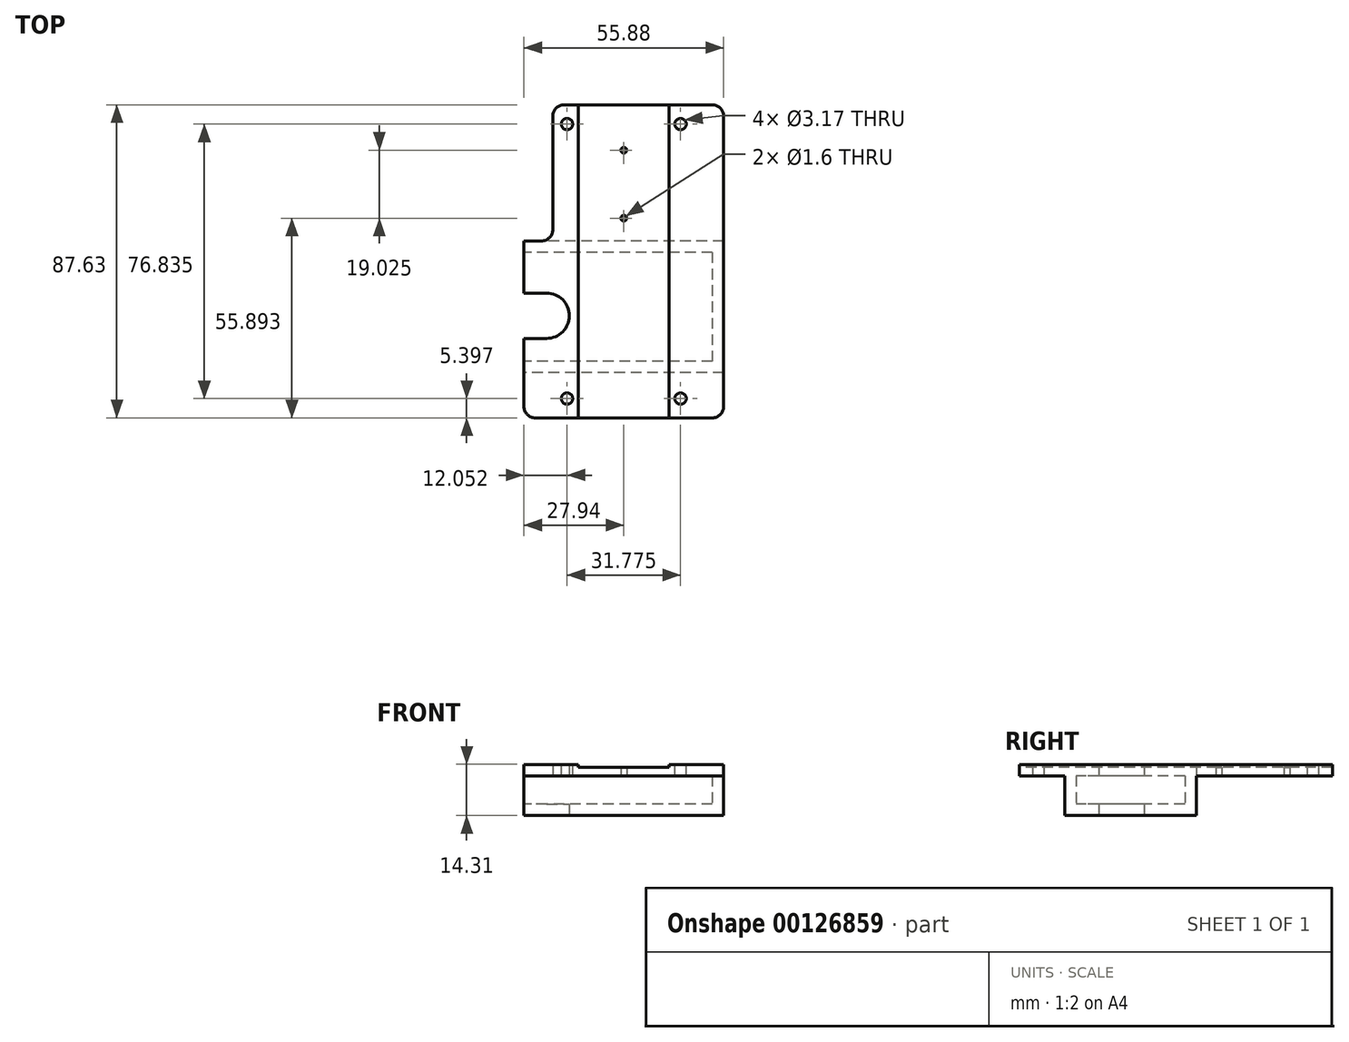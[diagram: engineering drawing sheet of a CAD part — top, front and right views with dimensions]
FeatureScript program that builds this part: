
annotation { "Feature Type Name" : "Feature", "Feature Type Description" : "" }
export const myFeature = defineFeature(function(context is Context, id is Id, definition is map)
    precondition{}
    {
        {
            var Q0;
            Q0=qCreatedBy(makeId("Top.planeOp"),FACE);
            var sketch = newSketch(context, id + "F0", { "sketchPlane" : qUnion([Q0])});
            skLineSegment(sketch, "E0.rect.top", {"start": v(27.94, 0) * mm, "end": v(-27.94, 0) * mm});
            skLineSegment(sketch, "E0.rect.left", {"start": v(27.94, 74.93) * mm, "end": v(27.94, 0) * mm});
            skLineSegment(sketch, "E0.rect.right", {"start": v(-27.94, 36.83) * mm, "end": v(-27.94, 0) * mm});
            skPoint(sketch, "E0.rect.middle", {"position": v(0, 0) * mm});
            skLineSegment(sketch, "E1", {"start": v(-27.94, 36.83) * mm, "end": v(27.94, 36.83) * mm, "construction": true});
            skCircle(sketch, "E2", {"center": v(0, 43.2) * mm, "radius": 0.8 * mm});
            skCircle(sketch, "E3", {"center": v(0, 62.22) * mm, "radius": 0.8 * mm});
            skLineSegment(sketch, "E4", {"start": v(0, 43.2) * mm, "end": v(0, 62.22) * mm, "construction": true});
            skPoint(sketch, "E5", {"position": v(0, 52.7) * mm});
            skLineSegment(sketch, "E6.bottom", {"start": v(14.29, 65.4) * mm, "end": v(-14.29, 65.4) * mm, "construction": true});
            skLineSegment(sketch, "E6.top", {"start": v(14.29, 40) * mm, "end": v(-14.29, 40) * mm, "construction": true});
            skLineSegment(sketch, "E6.left", {"start": v(14.29, 65.4) * mm, "end": v(14.29, 40) * mm, "construction": true});
            skLineSegment(sketch, "E6.right", {"start": v(-14.29, 65.4) * mm, "end": v(-14.29, 40) * mm, "construction": true});
            skLineSegment(sketch, "E7", {"start": v(-19.88, 74.93) * mm, "end": v(27.94, 74.93) * mm});
            skLineSegment(sketch, "E8.bottom", {"start": v(-19.88, 36.83) * mm, "end": v(-27.94, 36.83) * mm});
            skLineSegment(sketch, "E8.left", {"start": v(-19.88, 36.83) * mm, "end": v(-19.88, 74.93) * mm});
            skSolve(sketch);
        }
        {
            var Q0;
            Q0=qSketchRegion(id+"F0",true);
            extrude(context, id + "F1", {"entities" : qUnion([Q0]), "depth" : 3.17 * mm});
        }
        {
            var Q0;
            Q0=makeQuery(id+"F1.opExtrude","CAP_FACE",FACE,{"disambiguationData":[OSD([sQuery(id+"F0.wireOp",EDGE,"E0.rect.bottom"),sQuery(id+"F0.wireOp",EDGE,"E0.rect.top"),sQuery(id+"F0.wireOp",EDGE,"E0.rect.left"),sQuery(id+"F0.wireOp",EDGE,"E0.rect.right")])],"isStart":true});
            var sketch = newSketch(context, id + "F2", { "sketchPlane" : qUnion([Q0])});
            skLineSegment(sketch, "E9.bottom", {"start": v(-27.94, 0) * mm, "end": v(27.94, 0) * mm});
            skLineSegment(sketch, "E9.top", {"start": v(-27.94, -36.83) * mm, "end": v(27.94, -36.83) * mm});
            skLineSegment(sketch, "E9.left", {"start": v(-27.94, 0) * mm, "end": v(-27.94, -36.83) * mm});
            skLineSegment(sketch, "E9.right", {"start": v(27.94, 0) * mm, "end": v(27.94, -36.83) * mm});
            skPoint(sketch, "E10", {"position": v(0, 0) * mm});
            skSolve(sketch);
        }
        {
            var Q0;
            Q0=qSketchRegion(id+"F2",true);
            extrude(context, id + "F3", {"entities" : qUnion([Q0]), "operationType" : NewBodyOperationType.ADD, "depth" : 11.13 * mm});
        }
        {
            var Q0;
            Q0=makeQuery(id+"F3.opExtrude","CAP_FACE",FACE,{"disambiguationData":[OSD([sQuery(id+"F2.wireOp",EDGE,"E9.bottom"),sQuery(id+"F2.wireOp",EDGE,"E9.top"),sQuery(id+"F2.wireOp",EDGE,"E9.left"),sQuery(id+"F2.wireOp",EDGE,"E9.right")])],"isStart":false});
            var sketch = newSketch(context, id + "F4", { "sketchPlane" : qUnion([Q0])});
            skLineSegment(sketch, "E11", {"start": v(-27.94, -22.23) * mm, "end": v(-27.94, -9.53) * mm});
            skLineSegment(sketch, "E12", {"start": v(-27.94, -9.52) * mm, "end": v(-21.6, -9.52) * mm});
            skLineSegment(sketch, "E13", {"start": v(-27.94, -22.22) * mm, "end": v(-21.6, -22.22) * mm});
            skArc(sketch, "E14", {"start": v(-21.6, -22.22) * mm, "mid": v(-15.24, -15.88) * mm, "end": v(-21.6, -9.53) * mm});
            skSolve(sketch);
        }
        {
            var Q0;
            Q0=qSketchRegion(id+"F4",true);
            extrude(context, id + "F5", {"entities" : qUnion([Q0]), "operationType" : NewBodyOperationType.REMOVE, "endBound" : BoundingType.THROUGH_ALL, "oppositeDirection" : true, "depth" : 25.4 * mm});
        }
        {
            var Q0;
            {var subQ0=sQuery(id+"F0.wireOp",EDGE,"E0.rect.right");var subQ1=sQuery(id+"F0.wireOp",EDGE,"E0.rect.top");var subQ2=sQuery(id+"F2.wireOp",EDGE,"E9.left");Q0=makeQuery(id+"F5.boolean.opBoolean","SPLIT",FACE,{"disambiguationData":[TD([makeQuery(id+"F1.opExtrude","SWEPT_FACE",FACE,{"disambiguationData":[OSD([subQ1])]})])],"derivedFrom":makeQuery(id+"F3.boolean.opBoolean","MERGE",FACE,{"derivedFrom":[makeQuery(id+"F1.opExtrude","SWEPT_FACE",FACE,{"disambiguationData":[OSD([subQ0])]}),makeQuery(id+"F3.opExtrude","SWEPT_FACE",FACE,{"disambiguationData":[OSD([subQ2])]})]})});}
            var sketch = newSketch(context, id + "F6", { "sketchPlane" : qUnion([Q0])});
            skLineSegment(sketch, "E15.bottom", {"start": v(-33.66, 0) * mm, "end": v(-3.18, 0) * mm});
            skLineSegment(sketch, "E15.top", {"start": v(-33.66, -7.95) * mm, "end": v(-3.18, -7.95) * mm});
            skLineSegment(sketch, "E15.left", {"start": v(-33.66, 0) * mm, "end": v(-33.66, -7.95) * mm});
            skLineSegment(sketch, "E15.right", {"start": v(-3.18, 0) * mm, "end": v(-3.18, -7.95) * mm});
            skSolve(sketch);
        }
        {
            var Q0;
            Q0 = qSketchRegion(id + "F6", true);
            extrude(context, id + "F7", {"entities" : qUnion([Q0]), "operationType" : NewBodyOperationType.REMOVE, "oppositeDirection" : true, "depth" : 52.7 * mm});
        }
        {
            var Q0;
            Q0=makeQuery(id+"F3.boolean.opBoolean","MERGE",FACE,{"derivedFrom":[makeQuery(id+"F1.opExtrude","SWEPT_FACE",FACE,{"disambiguationData":[OSD([sQuery(id+"F0.wireOp",EDGE,"E0.rect.top")])]}),makeQuery(id+"F3.opExtrude","SWEPT_FACE",FACE,{"disambiguationData":[OSD([sQuery(id+"F2.wireOp",EDGE,"E9.bottom")])]})]});
            var sketch = newSketch(context, id + "F8", { "sketchPlane" : qUnion([Q0])});
            skLineSegment(sketch, "E16.bottom", {"start": v(-27.94, 3.18) * mm, "end": v(27.94, 3.18) * mm});
            skLineSegment(sketch, "E16.top", {"start": v(-27.94, 0) * mm, "end": v(27.94, 0) * mm});
            skLineSegment(sketch, "E16.left", {"start": v(-27.94, 3.18) * mm, "end": v(-27.94, 0) * mm});
            skLineSegment(sketch, "E16.right", {"start": v(27.94, 3.18) * mm, "end": v(27.94, 0) * mm});
            skSolve(sketch);
        }
        {
            var Q0;
            Q0 = qSketchRegion(id + "F8", true);
            extrude(context, id + "F9", {"entities" : qUnion([Q0]), "operationType" : NewBodyOperationType.ADD, "depth" : 12.7 * mm});
        }
        {
            var Q0;
            Q0=makeQuery(id+"F3.opExtrude","CAP_EDGE",EDGE,{"disambiguationData":[OSD([sQuery(id+"F2.wireOp",EDGE,"E9.top")])],"isStart":true});
            var Q1;
            Q1=makeQuery(id+"F1.opExtrude","SWEPT_EDGE",EDGE,{"disambiguationData":[OSD([sQuery(id+"F0.wireOp",EDGE,"E8.bottom"),sQuery(id+"F0.wireOp",EDGE,"E8.left")])]});
            var Q2;
            Q2=makeQuery(id+"F1.opExtrude","SWEPT_EDGE",EDGE,{"disambiguationData":[OSD([sQuery(id+"F0.wireOp",EDGE,"E7"),sQuery(id+"F0.wireOp",EDGE,"E8.left")])]});
            var Q3;
            Q3=makeQuery(id+"F1.opExtrude","SWEPT_EDGE",EDGE,{"disambiguationData":[OSD([sQuery(id+"F0.wireOp",EDGE,"E0.rect.left"),sQuery(id+"F0.wireOp",EDGE,"E7")])]});
            var Q4;
            Q4=makeQuery(id+"F9.opExtrude","CAP_EDGE",EDGE,{"disambiguationData":[OSD([sQuery(id+"F8.wireOp",EDGE,"E16.top")])],"isStart":true});
            var Q5;
            Q5=makeQuery(id+"F9.opExtrude","CAP_EDGE",EDGE,{"disambiguationData":[OSD([sQuery(id+"F8.wireOp",EDGE,"E16.left")])],"isStart":false});
            var Q6;
            Q6=makeQuery(id+"F9.opExtrude","CAP_EDGE",EDGE,{"disambiguationData":[OSD([sQuery(id+"F8.wireOp",EDGE,"E16.right")])],"isStart":false});
            fillet(context, id + "F10", {"entities" : qUnion([Q0, Q1, Q2, Q3, Q4, Q5, Q6]), "radius" : 3.17 * mm, "tangentPropagation" : true, "allowEdgeOverflow" : false});
        }
        {
            var Q0;
            {var subQ0=sQuery(id+"F0.wireOp",EDGE,"E7");var subQ1=sQuery(id+"F0.wireOp",EDGE,"E0.rect.left");var subQ2=sQuery(id+"F0.wireOp",EDGE,"E0.rect.top");Q0=makeQuery(id+"F14.boolean.opBoolean","SPLIT",FACE,{"disambiguationData":[TD([makeQuery(id+"F1.opExtrude","SWEPT_FACE",FACE,{"disambiguationData":[OSD([subQ1])]})])],"derivedFrom":makeQuery(id+"F1.opExtrude","CAP_FACE",FACE,{"disambiguationData":[OSD([subQ2,subQ1,sQuery(id+"F0.wireOp",EDGE,"E0.rect.right"),sQuery(id+"F0.wireOp",EDGE,"E2"),sQuery(id+"F0.wireOp",EDGE,"E3"),subQ0,sQuery(id+"F0.wireOp",EDGE,"E8.bottom"),sQuery(id+"F0.wireOp",EDGE,"E8.left")])],"isStart":false})});}
            var sketch = newSketch(context, id + "F11", { "sketchPlane" : qUnion([Q0])});
            skCircle(sketch, "E17", {"center": v(-15.89, 69.53) * mm, "radius": 1.59 * mm});
            skCircle(sketch, "E18", {"center": v(15.89, 69.53) * mm, "radius": 1.59 * mm});
            skCircle(sketch, "E19", {"center": v(-15.89, -7.3) * mm, "radius": 1.59 * mm});
            skCircle(sketch, "E20", {"center": v(15.89, -7.3) * mm, "radius": 1.59 * mm});
            skSolve(sketch);
        }
        {
            var Q0;
            Q0 = qSketchRegion(id + "F11", true);
            extrude(context, id + "F12", {"entities" : qUnion([Q0]), "operationType" : NewBodyOperationType.REMOVE, "endBound" : BoundingType.THROUGH_ALL, "oppositeDirection" : true, "depth" : 25.4 * mm});
        }
        {
            var Q0;
            Q0=makeQuery(id+"F9.opExtrude","CAP_FACE",FACE,{"disambiguationData":[OSD([sQuery(id+"F8.wireOp",EDGE,"E16.bottom"),sQuery(id+"F8.wireOp",EDGE,"E16.top"),sQuery(id+"F8.wireOp",EDGE,"E16.left"),sQuery(id+"F8.wireOp",EDGE,"E16.right")])],"isStart":false});
            var sketch = newSketch(context, id + "F13", { "sketchPlane" : qUnion([Q0])});
            skLineSegment(sketch, "E21.bottom", {"start": v(12.7, 3.98) * mm, "end": v(-12.7, 3.98) * mm});
            skLineSegment(sketch, "E21.top", {"start": v(12.7, 2.37) * mm, "end": v(-12.7, 2.37) * mm});
            skLineSegment(sketch, "E21.left", {"start": v(12.7, 3.98) * mm, "end": v(12.7, 2.37) * mm});
            skLineSegment(sketch, "E21.right", {"start": v(-12.7, 3.98) * mm, "end": v(-12.7, 2.37) * mm});
            skPoint(sketch, "E21.middle", {"position": v(0, 3.18) * mm});
            skSolve(sketch);
        }
        {
            var Q0;
            Q0=qSketchRegion(id+"F13",true);
            extrude(context, id + "F14", {"entities" : qUnion([Q0]), "operationType" : NewBodyOperationType.REMOVE, "endBound" : BoundingType.THROUGH_ALL, "oppositeDirection" : true, "depth" : 152.4 * mm});
        }
    });
